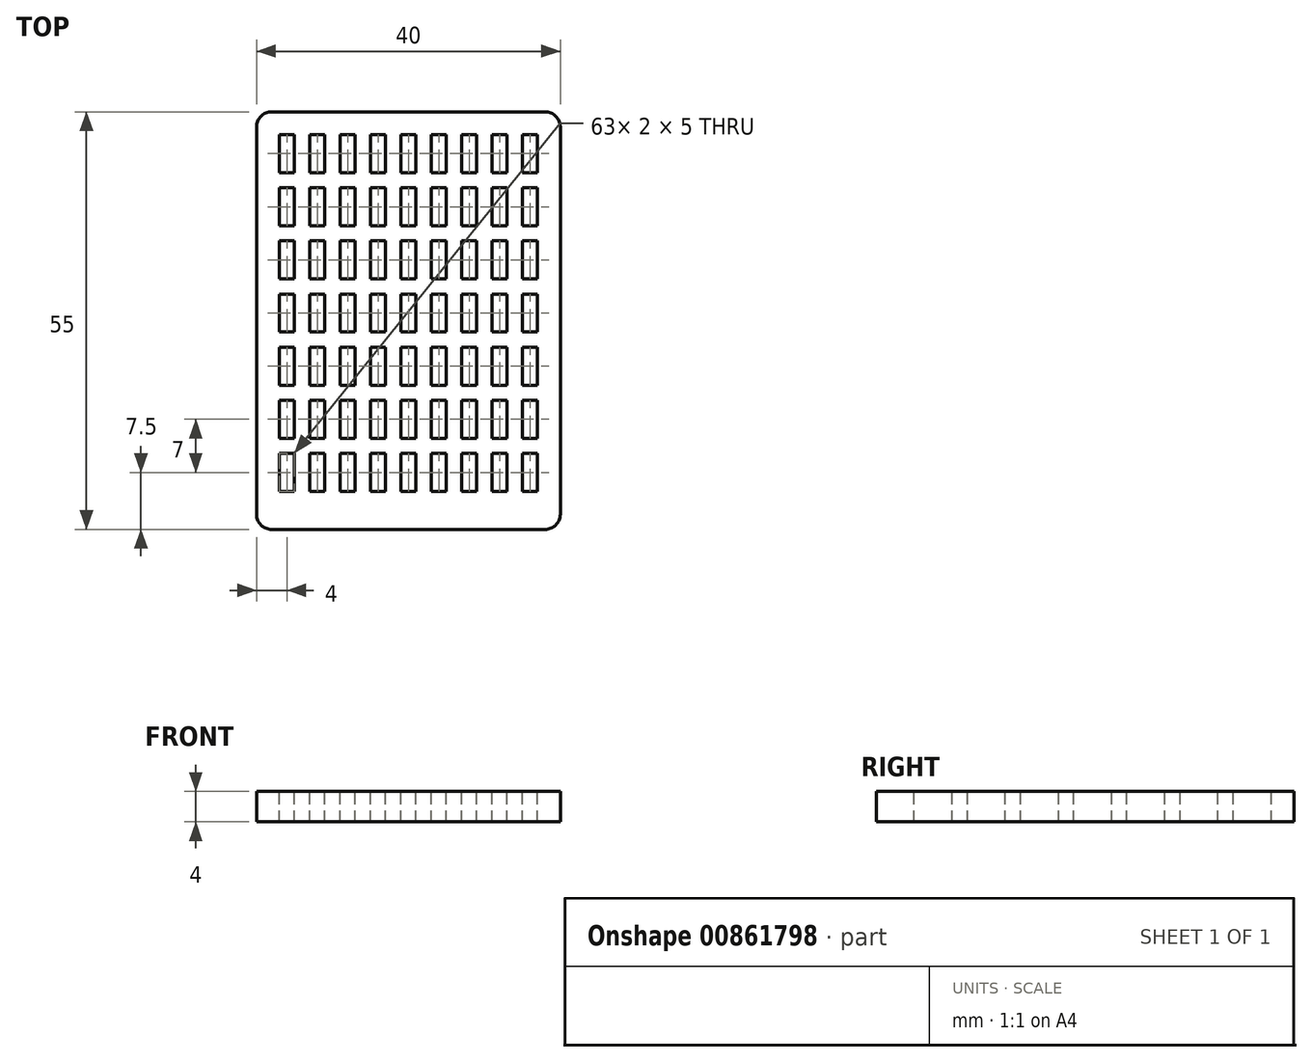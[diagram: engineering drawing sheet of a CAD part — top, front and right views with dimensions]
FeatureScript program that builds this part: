
annotation { "Feature Type Name" : "Feature", "Feature Type Description" : "" }
export const myFeature = defineFeature(function(context is Context, id is Id, definition is map)
    precondition{}
    {
        {
            var Q0;
            Q0=qCreatedBy(makeId("Top.planeOp"),FACE);
            var sketch = newSketch(context, id + "F0", { "sketchPlane" : qUnion([Q0])});
            skLineSegment(sketch, "E0.bottom", {"start": v(-20, 27.5) * mm, "end": v(20, 27.5) * mm});
            skLineSegment(sketch, "E0.top", {"start": v(-20, -27.5) * mm, "end": v(20, -27.5) * mm});
            skLineSegment(sketch, "E0.left", {"start": v(-20, 27.5) * mm, "end": v(-20, -27.5) * mm});
            skLineSegment(sketch, "E0.right", {"start": v(20, 27.5) * mm, "end": v(20, -27.5) * mm});
            skPoint(sketch, "E0.middle", {"position": v(0, 0) * mm});
            skSolve(sketch);
        }
        {
            var Q0;
            Q0=qSketchRegion(id+"F0",true);
            extrude(context, id + "F1", {"entities" : qUnion([Q0]), "depth" : 4 * mm, "offsetDistance" : 25 * mm});
        }
        {
            var Q0;
            Q0=makeQuery(id+"F1.opExtrude","SWEPT_EDGE",EDGE,{"disambiguationData":[OSD([sQuery(id+"F0.wireOp",EDGE,"E0.bottom"),sQuery(id+"F0.wireOp",EDGE,"E0.left")])]});
            var Q1;
            Q1=makeQuery(id+"F1.opExtrude","SWEPT_EDGE",EDGE,{"disambiguationData":[OSD([sQuery(id+"F0.wireOp",EDGE,"E0.bottom"),sQuery(id+"F0.wireOp",EDGE,"E0.right")])]});
            var Q2;
            Q2=makeQuery(id+"F1.opExtrude","SWEPT_EDGE",EDGE,{"disambiguationData":[OSD([sQuery(id+"F0.wireOp",EDGE,"E0.top"),sQuery(id+"F0.wireOp",EDGE,"E0.left")])]});
            var Q3;
            Q3=makeQuery(id+"F1.opExtrude","SWEPT_EDGE",EDGE,{"disambiguationData":[OSD([sQuery(id+"F0.wireOp",EDGE,"E0.top"),sQuery(id+"F0.wireOp",EDGE,"E0.right")])]});
            fillet(context, id + "F2", {"entities" : qUnion([Q0, Q1, Q2, Q3]), "radius" : 2 * mm, "tangentPropagation" : true, "allowEdgeOverflow" : false});
        }
        {
            var Q0;
            Q0=makeQuery(id+"F1.opExtrude","CAP_FACE",FACE,{"disambiguationData":[OSD([sQuery(id+"F0.wireOp",EDGE,"E0.bottom"),sQuery(id+"F0.wireOp",EDGE,"E0.top"),sQuery(id+"F0.wireOp",EDGE,"E0.left"),sQuery(id+"F0.wireOp",EDGE,"E0.right")])],"isStart":false});
            var sketch = newSketch(context, id + "F3", { "sketchPlane" : qUnion([Q0])});
            skLineSegment(sketch, "E1.bottom", {"start": v(-17, 27.5) * mm, "end": v(-15, 27.5) * mm});
            skLineSegment(sketch, "E1.top", {"start": v(-17, -27.5) * mm, "end": v(-15, -27.5) * mm});
            skLineSegment(sketch, "E1.left", {"start": v(-17, 27.5) * mm, "end": v(-17, -27.5) * mm});
            skLineSegment(sketch, "E1.right", {"start": v(-15, 27.5) * mm, "end": v(-15, -27.5) * mm});
            skLineSegment(sketch, "E2.bottom", {"start": v(-13, -27.5) * mm, "end": v(-11, -27.5) * mm});
            skLineSegment(sketch, "E2.top", {"start": v(-13, 27.5) * mm, "end": v(-11, 27.5) * mm});
            skLineSegment(sketch, "E2.left", {"start": v(-13, -27.5) * mm, "end": v(-13, 27.5) * mm});
            skLineSegment(sketch, "E2.right", {"start": v(-11, -27.5) * mm, "end": v(-11, 27.5) * mm});
            skLineSegment(sketch, "E3.bottom", {"start": v(-9, 27.5) * mm, "end": v(-7, 27.5) * mm});
            skLineSegment(sketch, "E3.top", {"start": v(-9, -27.5) * mm, "end": v(-7, -27.5) * mm});
            skLineSegment(sketch, "E3.left", {"start": v(-9, 27.5) * mm, "end": v(-9, -27.5) * mm});
            skLineSegment(sketch, "E3.right", {"start": v(-7, 27.5) * mm, "end": v(-7, -27.5) * mm});
            skLineSegment(sketch, "E4.bottom", {"start": v(-5, -27.5) * mm, "end": v(-3, -27.5) * mm});
            skLineSegment(sketch, "E4.top", {"start": v(-5, 27.5) * mm, "end": v(-3, 27.5) * mm});
            skLineSegment(sketch, "E4.left", {"start": v(-5, -27.5) * mm, "end": v(-5, 27.5) * mm});
            skLineSegment(sketch, "E4.right", {"start": v(-3, -27.5) * mm, "end": v(-3, 27.5) * mm});
            skLineSegment(sketch, "E5.bottom", {"start": v(-1, 27.5) * mm, "end": v(1, 27.5) * mm});
            skLineSegment(sketch, "E5.top", {"start": v(-1, -27.5) * mm, "end": v(1, -27.5) * mm});
            skLineSegment(sketch, "E5.left", {"start": v(-1, 27.5) * mm, "end": v(-1, -27.5) * mm});
            skLineSegment(sketch, "E5.right", {"start": v(1, 27.5) * mm, "end": v(1, -27.5) * mm});
            skLineSegment(sketch, "E6.bottom", {"start": v(3, 27.5) * mm, "end": v(5, 27.5) * mm});
            skLineSegment(sketch, "E6.top", {"start": v(3, -27.5) * mm, "end": v(5, -27.5) * mm});
            skLineSegment(sketch, "E6.left", {"start": v(3, 27.5) * mm, "end": v(3, -27.5) * mm});
            skLineSegment(sketch, "E6.right", {"start": v(5, 27.5) * mm, "end": v(5, -27.5) * mm});
            skLineSegment(sketch, "E7.bottom", {"start": v(7, -27.5) * mm, "end": v(9, -27.5) * mm});
            skLineSegment(sketch, "E7.top", {"start": v(7, 27.5) * mm, "end": v(9, 27.5) * mm});
            skLineSegment(sketch, "E7.left", {"start": v(7, -27.5) * mm, "end": v(7, 27.5) * mm});
            skLineSegment(sketch, "E7.right", {"start": v(9, -27.5) * mm, "end": v(9, 27.5) * mm});
            skLineSegment(sketch, "E8.bottom", {"start": v(11, 27.5) * mm, "end": v(13, 27.5) * mm});
            skLineSegment(sketch, "E8.top", {"start": v(11, -27.5) * mm, "end": v(13, -27.5) * mm});
            skLineSegment(sketch, "E8.left", {"start": v(11, 27.5) * mm, "end": v(11, -27.5) * mm});
            skLineSegment(sketch, "E8.right", {"start": v(13, 27.5) * mm, "end": v(13, -27.5) * mm});
            skLineSegment(sketch, "E9.bottom", {"start": v(15, -27.5) * mm, "end": v(17, -27.5) * mm});
            skLineSegment(sketch, "E9.top", {"start": v(15, 27.5) * mm, "end": v(17, 27.5) * mm});
            skLineSegment(sketch, "E9.left", {"start": v(15, -27.5) * mm, "end": v(15, 27.5) * mm});
            skLineSegment(sketch, "E9.right", {"start": v(17, -27.5) * mm, "end": v(17, 27.5) * mm});
            skLineSegment(sketch, "E10.bottom", {"start": v(-20, 24.5) * mm, "end": v(20, 24.5) * mm});
            skLineSegment(sketch, "E10.top", {"start": v(-20, 19.5) * mm, "end": v(20, 19.5) * mm});
            skLineSegment(sketch, "E10.left", {"start": v(-20, 24.5) * mm, "end": v(-20, 19.5) * mm});
            skLineSegment(sketch, "E10.right", {"start": v(20, 24.5) * mm, "end": v(20, 19.5) * mm});
            skLineSegment(sketch, "E11.bottom", {"start": v(-20, 17.5) * mm, "end": v(20, 17.5) * mm});
            skLineSegment(sketch, "E11.top", {"start": v(-20, 12.5) * mm, "end": v(20, 12.5) * mm});
            skLineSegment(sketch, "E11.left", {"start": v(-20, 17.5) * mm, "end": v(-20, 12.5) * mm});
            skLineSegment(sketch, "E11.right", {"start": v(20, 17.5) * mm, "end": v(20, 12.5) * mm});
            skLineSegment(sketch, "E12.bottom", {"start": v(-20, 10.5) * mm, "end": v(20, 10.5) * mm});
            skLineSegment(sketch, "E12.top", {"start": v(-20, 5.5) * mm, "end": v(20, 5.5) * mm});
            skLineSegment(sketch, "E12.left", {"start": v(-20, 10.5) * mm, "end": v(-20, 5.5) * mm});
            skLineSegment(sketch, "E12.right", {"start": v(20, 10.5) * mm, "end": v(20, 5.5) * mm});
            skLineSegment(sketch, "E13.bottom", {"start": v(-20, 3.5) * mm, "end": v(20, 3.5) * mm});
            skLineSegment(sketch, "E13.top", {"start": v(-20, -1.5) * mm, "end": v(20, -1.5) * mm});
            skLineSegment(sketch, "E13.left", {"start": v(-20, 3.5) * mm, "end": v(-20, -1.5) * mm});
            skLineSegment(sketch, "E13.right", {"start": v(20, 3.5) * mm, "end": v(20, -1.5) * mm});
            skLineSegment(sketch, "E14.bottom", {"start": v(-20, -3.5) * mm, "end": v(20, -3.5) * mm});
            skLineSegment(sketch, "E14.top", {"start": v(-20, -8.5) * mm, "end": v(20, -8.5) * mm});
            skLineSegment(sketch, "E14.left", {"start": v(-20, -3.5) * mm, "end": v(-20, -8.5) * mm});
            skLineSegment(sketch, "E14.right", {"start": v(20, -3.5) * mm, "end": v(20, -8.5) * mm});
            skLineSegment(sketch, "E15.bottom", {"start": v(20, -8.5) * mm, "end": v(-20, -8.5) * mm});
            skLineSegment(sketch, "E15.top", {"start": v(20, -10.5) * mm, "end": v(-20, -10.5) * mm});
            skLineSegment(sketch, "E15.left", {"start": v(20, -8.5) * mm, "end": v(20, -10.5) * mm});
            skLineSegment(sketch, "E15.right", {"start": v(-20, -8.5) * mm, "end": v(-20, -10.5) * mm});
            skLineSegment(sketch, "E16.bottom", {"start": v(-20, -15.5) * mm, "end": v(20, -15.5) * mm});
            skLineSegment(sketch, "E16.top", {"start": v(-20, -17.5) * mm, "end": v(20, -17.5) * mm});
            skLineSegment(sketch, "E16.left", {"start": v(-20, -15.5) * mm, "end": v(-20, -17.5) * mm});
            skLineSegment(sketch, "E16.right", {"start": v(20, -15.5) * mm, "end": v(20, -17.5) * mm});
            skLineSegment(sketch, "E17.bottom", {"start": v(20, -22.5) * mm, "end": v(-20, -22.5) * mm});
            skLineSegment(sketch, "E17.top", {"start": v(20, -24.5) * mm, "end": v(-20, -24.5) * mm});
            skLineSegment(sketch, "E17.left", {"start": v(20, -22.5) * mm, "end": v(20, -24.5) * mm});
            skLineSegment(sketch, "E17.right", {"start": v(-20, -22.5) * mm, "end": v(-20, -24.5) * mm});
            skSolve(sketch);
        }
        {
            var Q0;
            {var subQ0=sQuery(id+"F3.wireOp",EDGE,"E10.bottom");var subQ1=sQuery(id+"F3.wireOp",EDGE,"E1.left");var subQ2=makeQuery(id+"F3.imprint","INTERSECT",VERTEX,{"derivedFrom":[subQ1,subQ0]});Q0=makeQuery(id+"F3.imprint","IMPRINT",FACE,{"disambiguationData":[TD([[makeQuery(id+"F3.imprint","IMPRINT",EDGE,{"disambiguationData":[TD([[subQ2,-1.0]])],"derivedFrom":subQ1}),1.0]])]});}
            var Q1;
            {var subQ0=sQuery(id+"F3.wireOp",EDGE,"E11.bottom");var subQ1=sQuery(id+"F3.wireOp",EDGE,"E1.left");var subQ2=makeQuery(id+"F3.imprint","INTERSECT",VERTEX,{"derivedFrom":[subQ1,subQ0]});Q1=makeQuery(id+"F3.imprint","IMPRINT",FACE,{"disambiguationData":[TD([[makeQuery(id+"F3.imprint","IMPRINT",EDGE,{"disambiguationData":[TD([[subQ2,-1.0]])],"derivedFrom":subQ1}),1.0]])]});}
            var Q2;
            {var subQ0=sQuery(id+"F3.wireOp",EDGE,"E12.bottom");var subQ1=sQuery(id+"F3.wireOp",EDGE,"E1.left");var subQ2=makeQuery(id+"F3.imprint","INTERSECT",VERTEX,{"derivedFrom":[subQ1,subQ0]});Q2=makeQuery(id+"F3.imprint","IMPRINT",FACE,{"disambiguationData":[TD([[makeQuery(id+"F3.imprint","IMPRINT",EDGE,{"disambiguationData":[TD([[subQ2,-1.0]])],"derivedFrom":subQ1}),1.0]])]});}
            var Q3;
            {var subQ0=sQuery(id+"F3.wireOp",EDGE,"E13.bottom");var subQ1=sQuery(id+"F3.wireOp",EDGE,"E1.left");var subQ2=makeQuery(id+"F3.imprint","INTERSECT",VERTEX,{"derivedFrom":[subQ1,subQ0]});Q3=makeQuery(id+"F3.imprint","IMPRINT",FACE,{"disambiguationData":[TD([[makeQuery(id+"F3.imprint","IMPRINT",EDGE,{"disambiguationData":[TD([[subQ2,-1.0]])],"derivedFrom":subQ1}),1.0]])]});}
            var Q4;
            {var subQ0=sQuery(id+"F3.wireOp",EDGE,"E14.bottom");var subQ1=sQuery(id+"F3.wireOp",EDGE,"E1.left");var subQ2=makeQuery(id+"F3.imprint","INTERSECT",VERTEX,{"derivedFrom":[subQ1,subQ0]});Q4=makeQuery(id+"F3.imprint","IMPRINT",FACE,{"disambiguationData":[TD([[makeQuery(id+"F3.imprint","IMPRINT",EDGE,{"disambiguationData":[TD([[subQ2,-1.0]])],"derivedFrom":subQ1}),1.0]])]});}
            var Q5;
            {var subQ0=sQuery(id+"F3.wireOp",EDGE,"E15.top");var subQ1=sQuery(id+"F3.wireOp",EDGE,"E1.left");var subQ2=makeQuery(id+"F3.imprint","INTERSECT",VERTEX,{"derivedFrom":[subQ1,subQ0]});Q5=makeQuery(id+"F3.imprint","IMPRINT",FACE,{"disambiguationData":[TD([[makeQuery(id+"F3.imprint","IMPRINT",EDGE,{"disambiguationData":[TD([[subQ2,-1.0]])],"derivedFrom":subQ1}),1.0]])]});}
            var Q6;
            {var subQ0=sQuery(id+"F3.wireOp",EDGE,"E17.bottom");var subQ1=sQuery(id+"F3.wireOp",EDGE,"E2.left");var subQ2=makeQuery(id+"F3.imprint","INTERSECT",VERTEX,{"derivedFrom":[subQ1,subQ0]});Q6=makeQuery(id+"F3.imprint","IMPRINT",FACE,{"disambiguationData":[TD([[makeQuery(id+"F3.imprint","IMPRINT",EDGE,{"disambiguationData":[TD([[subQ2,-1.0]])],"derivedFrom":subQ1}),-1.0]])]});}
            var Q7;
            {var subQ0=sQuery(id+"F3.wireOp",EDGE,"E16.bottom");var subQ1=sQuery(id+"F3.wireOp",EDGE,"E2.left");var subQ2=makeQuery(id+"F3.imprint","INTERSECT",VERTEX,{"derivedFrom":[subQ1,subQ0]});Q7=makeQuery(id+"F3.imprint","IMPRINT",FACE,{"disambiguationData":[TD([[makeQuery(id+"F3.imprint","IMPRINT",EDGE,{"disambiguationData":[TD([[subQ2,-1.0]])],"derivedFrom":subQ1}),-1.0]])]});}
            var Q8;
            {var subQ0=sQuery(id+"F3.wireOp",EDGE,"E15.bottom");var subQ1=sQuery(id+"F3.wireOp",EDGE,"E2.left");var subQ2=makeQuery(id+"F3.imprint","INTERSECT",VERTEX,{"derivedFrom":[subQ1,subQ0]});Q8=makeQuery(id+"F3.imprint","IMPRINT",FACE,{"disambiguationData":[TD([[makeQuery(id+"F3.imprint","IMPRINT",EDGE,{"disambiguationData":[TD([[subQ2,-1.0]])],"derivedFrom":subQ1}),-1.0]])]});}
            var Q9;
            {var subQ0=sQuery(id+"F3.wireOp",EDGE,"E13.top");var subQ1=sQuery(id+"F3.wireOp",EDGE,"E2.left");var subQ2=makeQuery(id+"F3.imprint","INTERSECT",VERTEX,{"derivedFrom":[subQ1,subQ0]});Q9=makeQuery(id+"F3.imprint","IMPRINT",FACE,{"disambiguationData":[TD([[makeQuery(id+"F3.imprint","IMPRINT",EDGE,{"disambiguationData":[TD([[subQ2,-1.0]])],"derivedFrom":subQ1}),-1.0]])]});}
            var Q10;
            {var subQ0=sQuery(id+"F3.wireOp",EDGE,"E12.top");var subQ1=sQuery(id+"F3.wireOp",EDGE,"E2.left");var subQ2=makeQuery(id+"F3.imprint","INTERSECT",VERTEX,{"derivedFrom":[subQ1,subQ0]});Q10=makeQuery(id+"F3.imprint","IMPRINT",FACE,{"disambiguationData":[TD([[makeQuery(id+"F3.imprint","IMPRINT",EDGE,{"disambiguationData":[TD([[subQ2,-1.0]])],"derivedFrom":subQ1}),-1.0]])]});}
            var Q11;
            {var subQ0=sQuery(id+"F3.wireOp",EDGE,"E11.top");var subQ1=sQuery(id+"F3.wireOp",EDGE,"E2.left");var subQ2=makeQuery(id+"F3.imprint","INTERSECT",VERTEX,{"derivedFrom":[subQ1,subQ0]});Q11=makeQuery(id+"F3.imprint","IMPRINT",FACE,{"disambiguationData":[TD([[makeQuery(id+"F3.imprint","IMPRINT",EDGE,{"disambiguationData":[TD([[subQ2,-1.0]])],"derivedFrom":subQ1}),-1.0]])]});}
            var Q12;
            {var subQ0=sQuery(id+"F3.wireOp",EDGE,"E10.top");var subQ1=sQuery(id+"F3.wireOp",EDGE,"E2.left");var subQ2=makeQuery(id+"F3.imprint","INTERSECT",VERTEX,{"derivedFrom":[subQ1,subQ0]});Q12=makeQuery(id+"F3.imprint","IMPRINT",FACE,{"disambiguationData":[TD([[makeQuery(id+"F3.imprint","IMPRINT",EDGE,{"disambiguationData":[TD([[subQ2,-1.0]])],"derivedFrom":subQ1}),-1.0]])]});}
            var Q13;
            {var subQ0=sQuery(id+"F3.wireOp",EDGE,"E10.bottom");var subQ1=sQuery(id+"F3.wireOp",EDGE,"E3.left");var subQ2=makeQuery(id+"F3.imprint","INTERSECT",VERTEX,{"derivedFrom":[subQ1,subQ0]});Q13=makeQuery(id+"F3.imprint","IMPRINT",FACE,{"disambiguationData":[TD([[makeQuery(id+"F3.imprint","IMPRINT",EDGE,{"disambiguationData":[TD([[subQ2,-1.0]])],"derivedFrom":subQ1}),1.0]])]});}
            var Q14;
            {var subQ0=sQuery(id+"F3.wireOp",EDGE,"E11.bottom");var subQ1=sQuery(id+"F3.wireOp",EDGE,"E3.left");var subQ2=makeQuery(id+"F3.imprint","INTERSECT",VERTEX,{"derivedFrom":[subQ1,subQ0]});Q14=makeQuery(id+"F3.imprint","IMPRINT",FACE,{"disambiguationData":[TD([[makeQuery(id+"F3.imprint","IMPRINT",EDGE,{"disambiguationData":[TD([[subQ2,-1.0]])],"derivedFrom":subQ1}),1.0]])]});}
            var Q15;
            {var subQ0=sQuery(id+"F3.wireOp",EDGE,"E12.bottom");var subQ1=sQuery(id+"F3.wireOp",EDGE,"E3.left");var subQ2=makeQuery(id+"F3.imprint","INTERSECT",VERTEX,{"derivedFrom":[subQ1,subQ0]});Q15=makeQuery(id+"F3.imprint","IMPRINT",FACE,{"disambiguationData":[TD([[makeQuery(id+"F3.imprint","IMPRINT",EDGE,{"disambiguationData":[TD([[subQ2,-1.0]])],"derivedFrom":subQ1}),1.0]])]});}
            var Q16;
            {var subQ0=sQuery(id+"F3.wireOp",EDGE,"E13.bottom");var subQ1=sQuery(id+"F3.wireOp",EDGE,"E3.left");var subQ2=makeQuery(id+"F3.imprint","INTERSECT",VERTEX,{"derivedFrom":[subQ1,subQ0]});Q16=makeQuery(id+"F3.imprint","IMPRINT",FACE,{"disambiguationData":[TD([[makeQuery(id+"F3.imprint","IMPRINT",EDGE,{"disambiguationData":[TD([[subQ2,-1.0]])],"derivedFrom":subQ1}),1.0]])]});}
            var Q17;
            {var subQ0=sQuery(id+"F3.wireOp",EDGE,"E14.bottom");var subQ1=sQuery(id+"F3.wireOp",EDGE,"E3.left");var subQ2=makeQuery(id+"F3.imprint","INTERSECT",VERTEX,{"derivedFrom":[subQ1,subQ0]});Q17=makeQuery(id+"F3.imprint","IMPRINT",FACE,{"disambiguationData":[TD([[makeQuery(id+"F3.imprint","IMPRINT",EDGE,{"disambiguationData":[TD([[subQ2,-1.0]])],"derivedFrom":subQ1}),1.0]])]});}
            var Q18;
            {var subQ0=sQuery(id+"F3.wireOp",EDGE,"E15.top");var subQ1=sQuery(id+"F3.wireOp",EDGE,"E3.left");var subQ2=makeQuery(id+"F3.imprint","INTERSECT",VERTEX,{"derivedFrom":[subQ1,subQ0]});Q18=makeQuery(id+"F3.imprint","IMPRINT",FACE,{"disambiguationData":[TD([[makeQuery(id+"F3.imprint","IMPRINT",EDGE,{"disambiguationData":[TD([[subQ2,-1.0]])],"derivedFrom":subQ1}),1.0]])]});}
            var Q19;
            {var subQ0=sQuery(id+"F3.wireOp",EDGE,"E16.top");var subQ1=sQuery(id+"F3.wireOp",EDGE,"E1.left");var subQ2=makeQuery(id+"F3.imprint","INTERSECT",VERTEX,{"derivedFrom":[subQ1,subQ0]});Q19=makeQuery(id+"F3.imprint","IMPRINT",FACE,{"disambiguationData":[TD([[makeQuery(id+"F3.imprint","IMPRINT",EDGE,{"disambiguationData":[TD([[subQ2,-1.0]])],"derivedFrom":subQ1}),1.0]])]});}
            var Q20;
            {var subQ0=sQuery(id+"F3.wireOp",EDGE,"E16.top");var subQ1=sQuery(id+"F3.wireOp",EDGE,"E3.left");var subQ2=makeQuery(id+"F3.imprint","INTERSECT",VERTEX,{"derivedFrom":[subQ1,subQ0]});Q20=makeQuery(id+"F3.imprint","IMPRINT",FACE,{"disambiguationData":[TD([[makeQuery(id+"F3.imprint","IMPRINT",EDGE,{"disambiguationData":[TD([[subQ2,-1.0]])],"derivedFrom":subQ1}),1.0]])]});}
            var Q21;
            {var subQ0=sQuery(id+"F3.wireOp",EDGE,"E17.bottom");var subQ1=sQuery(id+"F3.wireOp",EDGE,"E4.left");var subQ2=makeQuery(id+"F3.imprint","INTERSECT",VERTEX,{"derivedFrom":[subQ1,subQ0]});Q21=makeQuery(id+"F3.imprint","IMPRINT",FACE,{"disambiguationData":[TD([[makeQuery(id+"F3.imprint","IMPRINT",EDGE,{"disambiguationData":[TD([[subQ2,-1.0]])],"derivedFrom":subQ1}),-1.0]])]});}
            var Q22;
            {var subQ0=sQuery(id+"F3.wireOp",EDGE,"E16.bottom");var subQ1=sQuery(id+"F3.wireOp",EDGE,"E4.left");var subQ2=makeQuery(id+"F3.imprint","INTERSECT",VERTEX,{"derivedFrom":[subQ1,subQ0]});Q22=makeQuery(id+"F3.imprint","IMPRINT",FACE,{"disambiguationData":[TD([[makeQuery(id+"F3.imprint","IMPRINT",EDGE,{"disambiguationData":[TD([[subQ2,-1.0]])],"derivedFrom":subQ1}),-1.0]])]});}
            var Q23;
            {var subQ0=sQuery(id+"F3.wireOp",EDGE,"E15.bottom");var subQ1=sQuery(id+"F3.wireOp",EDGE,"E4.left");var subQ2=makeQuery(id+"F3.imprint","INTERSECT",VERTEX,{"derivedFrom":[subQ1,subQ0]});Q23=makeQuery(id+"F3.imprint","IMPRINT",FACE,{"disambiguationData":[TD([[makeQuery(id+"F3.imprint","IMPRINT",EDGE,{"disambiguationData":[TD([[subQ2,-1.0]])],"derivedFrom":subQ1}),-1.0]])]});}
            var Q24;
            {var subQ0=sQuery(id+"F3.wireOp",EDGE,"E13.top");var subQ1=sQuery(id+"F3.wireOp",EDGE,"E4.left");var subQ2=makeQuery(id+"F3.imprint","INTERSECT",VERTEX,{"derivedFrom":[subQ1,subQ0]});Q24=makeQuery(id+"F3.imprint","IMPRINT",FACE,{"disambiguationData":[TD([[makeQuery(id+"F3.imprint","IMPRINT",EDGE,{"disambiguationData":[TD([[subQ2,-1.0]])],"derivedFrom":subQ1}),-1.0]])]});}
            var Q25;
            {var subQ0=sQuery(id+"F3.wireOp",EDGE,"E12.top");var subQ1=sQuery(id+"F3.wireOp",EDGE,"E4.left");var subQ2=makeQuery(id+"F3.imprint","INTERSECT",VERTEX,{"derivedFrom":[subQ1,subQ0]});Q25=makeQuery(id+"F3.imprint","IMPRINT",FACE,{"disambiguationData":[TD([[makeQuery(id+"F3.imprint","IMPRINT",EDGE,{"disambiguationData":[TD([[subQ2,-1.0]])],"derivedFrom":subQ1}),-1.0]])]});}
            var Q26;
            {var subQ0=sQuery(id+"F3.wireOp",EDGE,"E11.top");var subQ1=sQuery(id+"F3.wireOp",EDGE,"E4.left");var subQ2=makeQuery(id+"F3.imprint","INTERSECT",VERTEX,{"derivedFrom":[subQ1,subQ0]});Q26=makeQuery(id+"F3.imprint","IMPRINT",FACE,{"disambiguationData":[TD([[makeQuery(id+"F3.imprint","IMPRINT",EDGE,{"disambiguationData":[TD([[subQ2,-1.0]])],"derivedFrom":subQ1}),-1.0]])]});}
            var Q27;
            {var subQ0=sQuery(id+"F3.wireOp",EDGE,"E10.top");var subQ1=sQuery(id+"F3.wireOp",EDGE,"E4.left");var subQ2=makeQuery(id+"F3.imprint","INTERSECT",VERTEX,{"derivedFrom":[subQ1,subQ0]});Q27=makeQuery(id+"F3.imprint","IMPRINT",FACE,{"disambiguationData":[TD([[makeQuery(id+"F3.imprint","IMPRINT",EDGE,{"disambiguationData":[TD([[subQ2,-1.0]])],"derivedFrom":subQ1}),-1.0]])]});}
            var Q28;
            {var subQ0=sQuery(id+"F3.wireOp",EDGE,"E10.bottom");var subQ1=sQuery(id+"F3.wireOp",EDGE,"E5.left");var subQ2=makeQuery(id+"F3.imprint","INTERSECT",VERTEX,{"derivedFrom":[subQ1,subQ0]});Q28=makeQuery(id+"F3.imprint","IMPRINT",FACE,{"disambiguationData":[TD([[makeQuery(id+"F3.imprint","IMPRINT",EDGE,{"disambiguationData":[TD([[subQ2,-1.0]])],"derivedFrom":subQ1}),1.0]])]});}
            var Q29;
            {var subQ0=sQuery(id+"F3.wireOp",EDGE,"E11.bottom");var subQ1=sQuery(id+"F3.wireOp",EDGE,"E5.left");var subQ2=makeQuery(id+"F3.imprint","INTERSECT",VERTEX,{"derivedFrom":[subQ1,subQ0]});Q29=makeQuery(id+"F3.imprint","IMPRINT",FACE,{"disambiguationData":[TD([[makeQuery(id+"F3.imprint","IMPRINT",EDGE,{"disambiguationData":[TD([[subQ2,-1.0]])],"derivedFrom":subQ1}),1.0]])]});}
            var Q30;
            {var subQ0=sQuery(id+"F3.wireOp",EDGE,"E12.bottom");var subQ1=sQuery(id+"F3.wireOp",EDGE,"E5.left");var subQ2=makeQuery(id+"F3.imprint","INTERSECT",VERTEX,{"derivedFrom":[subQ1,subQ0]});Q30=makeQuery(id+"F3.imprint","IMPRINT",FACE,{"disambiguationData":[TD([[makeQuery(id+"F3.imprint","IMPRINT",EDGE,{"disambiguationData":[TD([[subQ2,-1.0]])],"derivedFrom":subQ1}),1.0]])]});}
            var Q31;
            {var subQ0=sQuery(id+"F3.wireOp",EDGE,"E13.bottom");var subQ1=sQuery(id+"F3.wireOp",EDGE,"E5.left");var subQ2=makeQuery(id+"F3.imprint","INTERSECT",VERTEX,{"derivedFrom":[subQ1,subQ0]});Q31=makeQuery(id+"F3.imprint","IMPRINT",FACE,{"disambiguationData":[TD([[makeQuery(id+"F3.imprint","IMPRINT",EDGE,{"disambiguationData":[TD([[subQ2,-1.0]])],"derivedFrom":subQ1}),1.0]])]});}
            var Q32;
            {var subQ0=sQuery(id+"F3.wireOp",EDGE,"E14.bottom");var subQ1=sQuery(id+"F3.wireOp",EDGE,"E5.left");var subQ2=makeQuery(id+"F3.imprint","INTERSECT",VERTEX,{"derivedFrom":[subQ1,subQ0]});Q32=makeQuery(id+"F3.imprint","IMPRINT",FACE,{"disambiguationData":[TD([[makeQuery(id+"F3.imprint","IMPRINT",EDGE,{"disambiguationData":[TD([[subQ2,-1.0]])],"derivedFrom":subQ1}),1.0]])]});}
            var Q33;
            {var subQ0=sQuery(id+"F3.wireOp",EDGE,"E15.top");var subQ1=sQuery(id+"F3.wireOp",EDGE,"E5.left");var subQ2=makeQuery(id+"F3.imprint","INTERSECT",VERTEX,{"derivedFrom":[subQ1,subQ0]});Q33=makeQuery(id+"F3.imprint","IMPRINT",FACE,{"disambiguationData":[TD([[makeQuery(id+"F3.imprint","IMPRINT",EDGE,{"disambiguationData":[TD([[subQ2,-1.0]])],"derivedFrom":subQ1}),1.0]])]});}
            var Q34;
            {var subQ0=sQuery(id+"F3.wireOp",EDGE,"E16.top");var subQ1=sQuery(id+"F3.wireOp",EDGE,"E5.left");var subQ2=makeQuery(id+"F3.imprint","INTERSECT",VERTEX,{"derivedFrom":[subQ1,subQ0]});Q34=makeQuery(id+"F3.imprint","IMPRINT",FACE,{"disambiguationData":[TD([[makeQuery(id+"F3.imprint","IMPRINT",EDGE,{"disambiguationData":[TD([[subQ2,-1.0]])],"derivedFrom":subQ1}),1.0]])]});}
            var Q35;
            {var subQ0=sQuery(id+"F3.wireOp",EDGE,"E16.top");var subQ1=sQuery(id+"F3.wireOp",EDGE,"E6.left");var subQ2=makeQuery(id+"F3.imprint","INTERSECT",VERTEX,{"derivedFrom":[subQ1,subQ0]});Q35=makeQuery(id+"F3.imprint","IMPRINT",FACE,{"disambiguationData":[TD([[makeQuery(id+"F3.imprint","IMPRINT",EDGE,{"disambiguationData":[TD([[subQ2,-1.0]])],"derivedFrom":subQ1}),1.0]])]});}
            var Q36;
            {var subQ0=sQuery(id+"F3.wireOp",EDGE,"E15.top");var subQ1=sQuery(id+"F3.wireOp",EDGE,"E6.left");var subQ2=makeQuery(id+"F3.imprint","INTERSECT",VERTEX,{"derivedFrom":[subQ1,subQ0]});Q36=makeQuery(id+"F3.imprint","IMPRINT",FACE,{"disambiguationData":[TD([[makeQuery(id+"F3.imprint","IMPRINT",EDGE,{"disambiguationData":[TD([[subQ2,-1.0]])],"derivedFrom":subQ1}),1.0]])]});}
            var Q37;
            {var subQ0=sQuery(id+"F3.wireOp",EDGE,"E14.bottom");var subQ1=sQuery(id+"F3.wireOp",EDGE,"E6.left");var subQ2=makeQuery(id+"F3.imprint","INTERSECT",VERTEX,{"derivedFrom":[subQ1,subQ0]});Q37=makeQuery(id+"F3.imprint","IMPRINT",FACE,{"disambiguationData":[TD([[makeQuery(id+"F3.imprint","IMPRINT",EDGE,{"disambiguationData":[TD([[subQ2,-1.0]])],"derivedFrom":subQ1}),1.0]])]});}
            var Q38;
            {var subQ0=sQuery(id+"F3.wireOp",EDGE,"E13.bottom");var subQ1=sQuery(id+"F3.wireOp",EDGE,"E6.left");var subQ2=makeQuery(id+"F3.imprint","INTERSECT",VERTEX,{"derivedFrom":[subQ1,subQ0]});Q38=makeQuery(id+"F3.imprint","IMPRINT",FACE,{"disambiguationData":[TD([[makeQuery(id+"F3.imprint","IMPRINT",EDGE,{"disambiguationData":[TD([[subQ2,-1.0]])],"derivedFrom":subQ1}),1.0]])]});}
            var Q39;
            {var subQ0=sQuery(id+"F3.wireOp",EDGE,"E12.bottom");var subQ1=sQuery(id+"F3.wireOp",EDGE,"E6.left");var subQ2=makeQuery(id+"F3.imprint","INTERSECT",VERTEX,{"derivedFrom":[subQ1,subQ0]});Q39=makeQuery(id+"F3.imprint","IMPRINT",FACE,{"disambiguationData":[TD([[makeQuery(id+"F3.imprint","IMPRINT",EDGE,{"disambiguationData":[TD([[subQ2,-1.0]])],"derivedFrom":subQ1}),1.0]])]});}
            var Q40;
            {var subQ0=sQuery(id+"F3.wireOp",EDGE,"E11.bottom");var subQ1=sQuery(id+"F3.wireOp",EDGE,"E6.left");var subQ2=makeQuery(id+"F3.imprint","INTERSECT",VERTEX,{"derivedFrom":[subQ1,subQ0]});Q40=makeQuery(id+"F3.imprint","IMPRINT",FACE,{"disambiguationData":[TD([[makeQuery(id+"F3.imprint","IMPRINT",EDGE,{"disambiguationData":[TD([[subQ2,-1.0]])],"derivedFrom":subQ1}),1.0]])]});}
            var Q41;
            {var subQ0=sQuery(id+"F3.wireOp",EDGE,"E10.bottom");var subQ1=sQuery(id+"F3.wireOp",EDGE,"E6.left");var subQ2=makeQuery(id+"F3.imprint","INTERSECT",VERTEX,{"derivedFrom":[subQ1,subQ0]});Q41=makeQuery(id+"F3.imprint","IMPRINT",FACE,{"disambiguationData":[TD([[makeQuery(id+"F3.imprint","IMPRINT",EDGE,{"disambiguationData":[TD([[subQ2,-1.0]])],"derivedFrom":subQ1}),1.0]])]});}
            var Q42;
            {var subQ0=sQuery(id+"F3.wireOp",EDGE,"E10.top");var subQ1=sQuery(id+"F3.wireOp",EDGE,"E7.left");var subQ2=makeQuery(id+"F3.imprint","INTERSECT",VERTEX,{"derivedFrom":[subQ1,subQ0]});Q42=makeQuery(id+"F3.imprint","IMPRINT",FACE,{"disambiguationData":[TD([[makeQuery(id+"F3.imprint","IMPRINT",EDGE,{"disambiguationData":[TD([[subQ2,-1.0]])],"derivedFrom":subQ1}),-1.0]])]});}
            var Q43;
            {var subQ0=sQuery(id+"F3.wireOp",EDGE,"E11.top");var subQ1=sQuery(id+"F3.wireOp",EDGE,"E7.left");var subQ2=makeQuery(id+"F3.imprint","INTERSECT",VERTEX,{"derivedFrom":[subQ1,subQ0]});Q43=makeQuery(id+"F3.imprint","IMPRINT",FACE,{"disambiguationData":[TD([[makeQuery(id+"F3.imprint","IMPRINT",EDGE,{"disambiguationData":[TD([[subQ2,-1.0]])],"derivedFrom":subQ1}),-1.0]])]});}
            var Q44;
            {var subQ0=sQuery(id+"F3.wireOp",EDGE,"E12.top");var subQ1=sQuery(id+"F3.wireOp",EDGE,"E7.left");var subQ2=makeQuery(id+"F3.imprint","INTERSECT",VERTEX,{"derivedFrom":[subQ1,subQ0]});Q44=makeQuery(id+"F3.imprint","IMPRINT",FACE,{"disambiguationData":[TD([[makeQuery(id+"F3.imprint","IMPRINT",EDGE,{"disambiguationData":[TD([[subQ2,-1.0]])],"derivedFrom":subQ1}),-1.0]])]});}
            var Q45;
            {var subQ0=sQuery(id+"F3.wireOp",EDGE,"E13.top");var subQ1=sQuery(id+"F3.wireOp",EDGE,"E7.left");var subQ2=makeQuery(id+"F3.imprint","INTERSECT",VERTEX,{"derivedFrom":[subQ1,subQ0]});Q45=makeQuery(id+"F3.imprint","IMPRINT",FACE,{"disambiguationData":[TD([[makeQuery(id+"F3.imprint","IMPRINT",EDGE,{"disambiguationData":[TD([[subQ2,-1.0]])],"derivedFrom":subQ1}),-1.0]])]});}
            var Q46;
            {var subQ0=sQuery(id+"F3.wireOp",EDGE,"E15.bottom");var subQ1=sQuery(id+"F3.wireOp",EDGE,"E7.left");var subQ2=makeQuery(id+"F3.imprint","INTERSECT",VERTEX,{"derivedFrom":[subQ1,subQ0]});Q46=makeQuery(id+"F3.imprint","IMPRINT",FACE,{"disambiguationData":[TD([[makeQuery(id+"F3.imprint","IMPRINT",EDGE,{"disambiguationData":[TD([[subQ2,-1.0]])],"derivedFrom":subQ1}),-1.0]])]});}
            var Q47;
            {var subQ0=sQuery(id+"F3.wireOp",EDGE,"E16.bottom");var subQ1=sQuery(id+"F3.wireOp",EDGE,"E7.left");var subQ2=makeQuery(id+"F3.imprint","INTERSECT",VERTEX,{"derivedFrom":[subQ1,subQ0]});Q47=makeQuery(id+"F3.imprint","IMPRINT",FACE,{"disambiguationData":[TD([[makeQuery(id+"F3.imprint","IMPRINT",EDGE,{"disambiguationData":[TD([[subQ2,-1.0]])],"derivedFrom":subQ1}),-1.0]])]});}
            var Q48;
            {var subQ0=sQuery(id+"F3.wireOp",EDGE,"E17.bottom");var subQ1=sQuery(id+"F3.wireOp",EDGE,"E7.left");var subQ2=makeQuery(id+"F3.imprint","INTERSECT",VERTEX,{"derivedFrom":[subQ1,subQ0]});Q48=makeQuery(id+"F3.imprint","IMPRINT",FACE,{"disambiguationData":[TD([[makeQuery(id+"F3.imprint","IMPRINT",EDGE,{"disambiguationData":[TD([[subQ2,-1.0]])],"derivedFrom":subQ1}),-1.0]])]});}
            var Q49;
            {var subQ0=sQuery(id+"F3.wireOp",EDGE,"E16.top");var subQ1=sQuery(id+"F3.wireOp",EDGE,"E8.left");var subQ2=makeQuery(id+"F3.imprint","INTERSECT",VERTEX,{"derivedFrom":[subQ1,subQ0]});Q49=makeQuery(id+"F3.imprint","IMPRINT",FACE,{"disambiguationData":[TD([[makeQuery(id+"F3.imprint","IMPRINT",EDGE,{"disambiguationData":[TD([[subQ2,-1.0]])],"derivedFrom":subQ1}),1.0]])]});}
            var Q50;
            {var subQ0=sQuery(id+"F3.wireOp",EDGE,"E15.top");var subQ1=sQuery(id+"F3.wireOp",EDGE,"E8.left");var subQ2=makeQuery(id+"F3.imprint","INTERSECT",VERTEX,{"derivedFrom":[subQ1,subQ0]});Q50=makeQuery(id+"F3.imprint","IMPRINT",FACE,{"disambiguationData":[TD([[makeQuery(id+"F3.imprint","IMPRINT",EDGE,{"disambiguationData":[TD([[subQ2,-1.0]])],"derivedFrom":subQ1}),1.0]])]});}
            var Q51;
            {var subQ0=sQuery(id+"F3.wireOp",EDGE,"E14.bottom");var subQ1=sQuery(id+"F3.wireOp",EDGE,"E8.left");var subQ2=makeQuery(id+"F3.imprint","INTERSECT",VERTEX,{"derivedFrom":[subQ1,subQ0]});Q51=makeQuery(id+"F3.imprint","IMPRINT",FACE,{"disambiguationData":[TD([[makeQuery(id+"F3.imprint","IMPRINT",EDGE,{"disambiguationData":[TD([[subQ2,-1.0]])],"derivedFrom":subQ1}),1.0]])]});}
            var Q52;
            {var subQ0=sQuery(id+"F3.wireOp",EDGE,"E13.bottom");var subQ1=sQuery(id+"F3.wireOp",EDGE,"E8.left");var subQ2=makeQuery(id+"F3.imprint","INTERSECT",VERTEX,{"derivedFrom":[subQ1,subQ0]});Q52=makeQuery(id+"F3.imprint","IMPRINT",FACE,{"disambiguationData":[TD([[makeQuery(id+"F3.imprint","IMPRINT",EDGE,{"disambiguationData":[TD([[subQ2,-1.0]])],"derivedFrom":subQ1}),1.0]])]});}
            var Q53;
            {var subQ0=sQuery(id+"F3.wireOp",EDGE,"E12.bottom");var subQ1=sQuery(id+"F3.wireOp",EDGE,"E8.left");var subQ2=makeQuery(id+"F3.imprint","INTERSECT",VERTEX,{"derivedFrom":[subQ1,subQ0]});Q53=makeQuery(id+"F3.imprint","IMPRINT",FACE,{"disambiguationData":[TD([[makeQuery(id+"F3.imprint","IMPRINT",EDGE,{"disambiguationData":[TD([[subQ2,-1.0]])],"derivedFrom":subQ1}),1.0]])]});}
            var Q54;
            {var subQ0=sQuery(id+"F3.wireOp",EDGE,"E11.bottom");var subQ1=sQuery(id+"F3.wireOp",EDGE,"E8.left");var subQ2=makeQuery(id+"F3.imprint","INTERSECT",VERTEX,{"derivedFrom":[subQ1,subQ0]});Q54=makeQuery(id+"F3.imprint","IMPRINT",FACE,{"disambiguationData":[TD([[makeQuery(id+"F3.imprint","IMPRINT",EDGE,{"disambiguationData":[TD([[subQ2,-1.0]])],"derivedFrom":subQ1}),1.0]])]});}
            var Q55;
            {var subQ0=sQuery(id+"F3.wireOp",EDGE,"E10.bottom");var subQ1=sQuery(id+"F3.wireOp",EDGE,"E8.left");var subQ2=makeQuery(id+"F3.imprint","INTERSECT",VERTEX,{"derivedFrom":[subQ1,subQ0]});Q55=makeQuery(id+"F3.imprint","IMPRINT",FACE,{"disambiguationData":[TD([[makeQuery(id+"F3.imprint","IMPRINT",EDGE,{"disambiguationData":[TD([[subQ2,-1.0]])],"derivedFrom":subQ1}),1.0]])]});}
            var Q56;
            {var subQ0=sQuery(id+"F3.wireOp",EDGE,"E10.top");var subQ1=sQuery(id+"F3.wireOp",EDGE,"E9.left");var subQ2=makeQuery(id+"F3.imprint","INTERSECT",VERTEX,{"derivedFrom":[subQ1,subQ0]});Q56=makeQuery(id+"F3.imprint","IMPRINT",FACE,{"disambiguationData":[TD([[makeQuery(id+"F3.imprint","IMPRINT",EDGE,{"disambiguationData":[TD([[subQ2,-1.0]])],"derivedFrom":subQ1}),-1.0]])]});}
            var Q57;
            {var subQ0=sQuery(id+"F3.wireOp",EDGE,"E11.top");var subQ1=sQuery(id+"F3.wireOp",EDGE,"E9.left");var subQ2=makeQuery(id+"F3.imprint","INTERSECT",VERTEX,{"derivedFrom":[subQ1,subQ0]});Q57=makeQuery(id+"F3.imprint","IMPRINT",FACE,{"disambiguationData":[TD([[makeQuery(id+"F3.imprint","IMPRINT",EDGE,{"disambiguationData":[TD([[subQ2,-1.0]])],"derivedFrom":subQ1}),-1.0]])]});}
            var Q58;
            {var subQ0=sQuery(id+"F3.wireOp",EDGE,"E12.top");var subQ1=sQuery(id+"F3.wireOp",EDGE,"E9.left");var subQ2=makeQuery(id+"F3.imprint","INTERSECT",VERTEX,{"derivedFrom":[subQ1,subQ0]});Q58=makeQuery(id+"F3.imprint","IMPRINT",FACE,{"disambiguationData":[TD([[makeQuery(id+"F3.imprint","IMPRINT",EDGE,{"disambiguationData":[TD([[subQ2,-1.0]])],"derivedFrom":subQ1}),-1.0]])]});}
            var Q59;
            {var subQ0=sQuery(id+"F3.wireOp",EDGE,"E13.top");var subQ1=sQuery(id+"F3.wireOp",EDGE,"E9.left");var subQ2=makeQuery(id+"F3.imprint","INTERSECT",VERTEX,{"derivedFrom":[subQ1,subQ0]});Q59=makeQuery(id+"F3.imprint","IMPRINT",FACE,{"disambiguationData":[TD([[makeQuery(id+"F3.imprint","IMPRINT",EDGE,{"disambiguationData":[TD([[subQ2,-1.0]])],"derivedFrom":subQ1}),-1.0]])]});}
            var Q60;
            {var subQ0=sQuery(id+"F3.wireOp",EDGE,"E15.bottom");var subQ1=sQuery(id+"F3.wireOp",EDGE,"E9.left");var subQ2=makeQuery(id+"F3.imprint","INTERSECT",VERTEX,{"derivedFrom":[subQ1,subQ0]});Q60=makeQuery(id+"F3.imprint","IMPRINT",FACE,{"disambiguationData":[TD([[makeQuery(id+"F3.imprint","IMPRINT",EDGE,{"disambiguationData":[TD([[subQ2,-1.0]])],"derivedFrom":subQ1}),-1.0]])]});}
            var Q61;
            {var subQ0=sQuery(id+"F3.wireOp",EDGE,"E16.bottom");var subQ1=sQuery(id+"F3.wireOp",EDGE,"E9.left");var subQ2=makeQuery(id+"F3.imprint","INTERSECT",VERTEX,{"derivedFrom":[subQ1,subQ0]});Q61=makeQuery(id+"F3.imprint","IMPRINT",FACE,{"disambiguationData":[TD([[makeQuery(id+"F3.imprint","IMPRINT",EDGE,{"disambiguationData":[TD([[subQ2,-1.0]])],"derivedFrom":subQ1}),-1.0]])]});}
            var Q62;
            {var subQ0=sQuery(id+"F3.wireOp",EDGE,"E17.bottom");var subQ1=sQuery(id+"F3.wireOp",EDGE,"E9.left");var subQ2=makeQuery(id+"F3.imprint","INTERSECT",VERTEX,{"derivedFrom":[subQ1,subQ0]});Q62=makeQuery(id+"F3.imprint","IMPRINT",FACE,{"disambiguationData":[TD([[makeQuery(id+"F3.imprint","IMPRINT",EDGE,{"disambiguationData":[TD([[subQ2,-1.0]])],"derivedFrom":subQ1}),-1.0]])]});}
            extrude(context, id + "F4", {"entities" : qUnion([Q0, Q1, Q2, Q3, Q4, Q5, Q6, Q7, Q8, Q9, Q10, Q11, Q12, Q13, Q14, Q15, Q16, Q17, Q18, Q19, Q20, Q21, Q22, Q23, Q24, Q25, Q26, Q27, Q28, Q29, Q30, Q31, Q32, Q33, Q34, Q35, Q36, Q37, Q38, Q39, Q40, Q41, Q42, Q43, Q44, Q45, Q46, Q47, Q48, Q49, Q50, Q51, Q52, Q53, Q54, Q55, Q56, Q57, Q58, Q59, Q60, Q61, Q62]), "operationType" : NewBodyOperationType.REMOVE, "oppositeDirection" : true, "depth" : 4 * mm, "offsetDistance" : 25 * mm});
        }
    });
